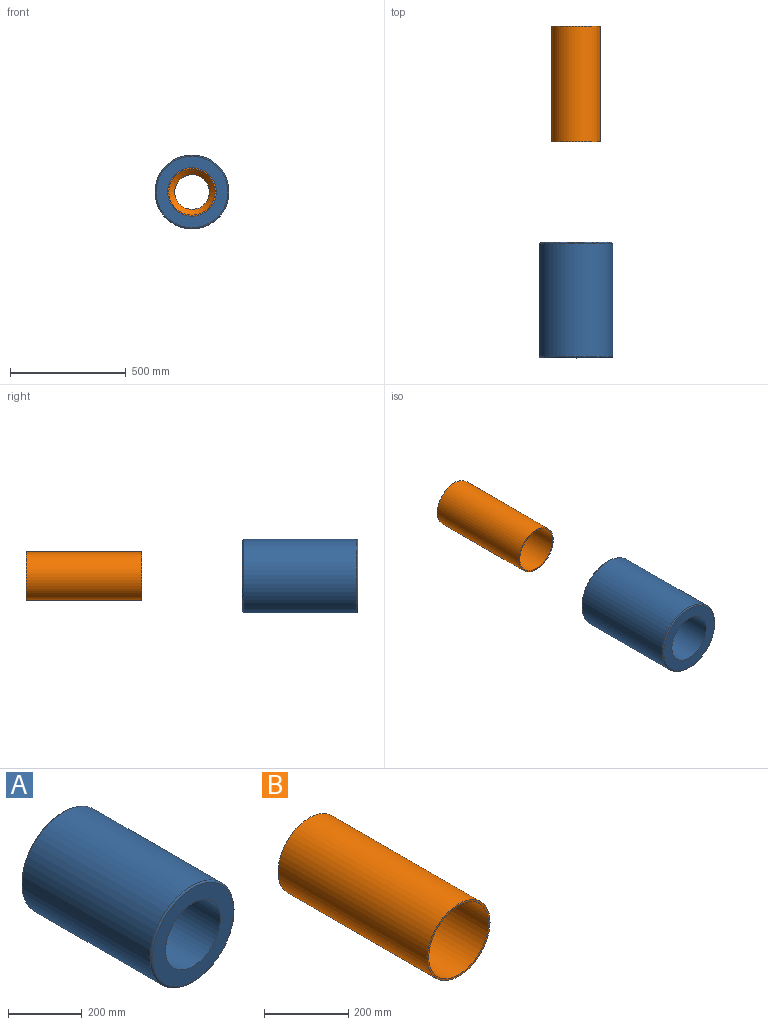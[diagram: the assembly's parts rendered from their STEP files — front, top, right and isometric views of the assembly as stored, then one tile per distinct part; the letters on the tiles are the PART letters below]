
ASSEMBLY  parts=2 mates=1
PART A: 6 faces, bbox 346.4x500x346.4 mm
  f0: cylinder r=160mm len=490mm, axis (0,1,0), area 492601.7mm2, adj f4,f5
  f1: plane 310x310mm, normal (0,-1,0), area 40840.7mm2, adj f3,f4
  f2: plane 310x310mm, normal (0,1,0), area 40840.7mm2, adj f3,f5
  f3: cylinder r=105mm len=500mm, axis (0,-1,0), area 329867.2mm2, adj f1,f2
  f4: torus R=155mm, axis (0,-1,0), area 7806mm2, adj f0,f1
  f5: cone r=160mm half-angle=45deg, axis (0,-1,0), area 6997.5mm2, adj f0,f2
PART B: 47 faces, bbox 210x500x210 mm
  f0: cylinder r=75mm len=315mm, axis (0,1,0), area 148440.3mm2, adj f45,f46
  f1: cylinder r=105mm len=500mm, axis (0,-1,0), area 329867.2mm2, adj f2,f3
  f2: plane 210x210mm, normal (0,-1,0), area 3220.1mm2, adj f1,f44
  f3: plane 210x210mm, normal (0,1,0), area 12075.5mm2, adj f1,f4,f6,f8,f10,f12,f14,f16
  f4: cylinder r=6.25mm len=300mm, axis (0,1,0), area 11781mm2, adj f3,f5
  f5: plane 12.5x12.5mm, normal (0,1,0), area 122.7mm2, adj f4
  f6: cylinder r=6.25mm len=300mm, axis (0,1,0), area 11781mm2, adj f3,f7
  f7: plane 12.5x12.5mm, normal (0,1,0), area 122.7mm2, adj f6
  f8: cylinder r=6.25mm len=300mm, axis (0,1,0), area 11781mm2, adj f3,f9
  f9: plane 12.5x12.5mm, normal (0,1,0), area 122.7mm2, adj f8
  f10: cylinder r=6.25mm len=300mm, axis (0,1,0), area 11781mm2, adj f3,f11
  f11: plane 12.5x12.5mm, normal (0,1,0), area 122.7mm2, adj f10
  f12: cylinder r=6.25mm len=300mm, axis (0,1,0), area 11781mm2, adj f3,f13
  f13: plane 12.5x12.5mm, normal (0,1,0), area 122.7mm2, adj f12
  f14: cylinder r=6.25mm len=300mm, axis (0,1,0), area 11781mm2, adj f3,f15
  f15: plane 12.5x12.5mm, normal (0,1,0), area 122.7mm2, adj f14
  f16: cylinder r=6.25mm len=300mm, axis (0,1,0), area 11781mm2, adj f3,f17
  f17: plane 12.5x12.5mm, normal (0,1,0), area 122.7mm2, adj f16
  f18: cylinder r=6.25mm len=300mm, axis (0,1,0), area 11781mm2, adj f3,f19
  f19: plane 12.5x12.5mm, normal (0,1,0), area 122.7mm2, adj f18
  f20: cylinder r=6.25mm len=300mm, axis (0,1,0), area 11781mm2, adj f3,f21
  f21: plane 12.5x12.5mm, normal (0,1,0), area 122.7mm2, adj f20
  f22: cylinder r=6.25mm len=300mm, axis (0,1,0), area 11781mm2, adj f3,f23
  f23: plane 12.5x12.5mm, normal (0,1,0), area 122.7mm2, adj f22
  f24: cylinder r=6.25mm len=300mm, axis (0,1,0), area 11781mm2, adj f3,f25
  f25: plane 12.5x12.5mm, normal (0,1,0), area 122.7mm2, adj f24
  f26: cylinder r=6.25mm len=300mm, axis (0,1,0), area 11781mm2, adj f3,f27
  f27: plane 12.5x12.5mm, normal (0,1,0), area 122.7mm2, adj f26
  f28: cylinder r=6.25mm len=300mm, axis (0,1,0), area 11781mm2, adj f3,f29
  f29: plane 12.5x12.5mm, normal (0,1,0), area 122.7mm2, adj f28
  f30: cylinder r=6.25mm len=300mm, axis (0,1,0), area 11781mm2, adj f3,f31
  f31: plane 12.5x12.5mm, normal (0,1,0), area 122.7mm2, adj f30
  f32: cylinder r=6.25mm len=300mm, axis (0,1,0), area 11781mm2, adj f3,f33
  f33: plane 12.5x12.5mm, normal (0,1,0), area 122.7mm2, adj f32
  f34: cylinder r=6.25mm len=300mm, axis (0,1,0), area 11781mm2, adj f3,f35
  f35: plane 12.5x12.5mm, normal (0,1,0), area 122.7mm2, adj f34
  f36: cylinder r=6.25mm len=300mm, axis (0,1,0), area 11781mm2, adj f3,f37
  f37: plane 12.5x12.5mm, normal (0,1,0), area 122.7mm2, adj f36
  f38: cylinder r=6.25mm len=300mm, axis (0,1,0), area 11781mm2, adj f3,f39
  f39: plane 12.5x12.5mm, normal (0,1,0), area 122.7mm2, adj f38
  f40: cylinder r=6.25mm len=300mm, axis (0,1,0), area 11781mm2, adj f3,f41
  f41: plane 12.5x12.5mm, normal (0,1,0), area 122.7mm2, adj f40
  f42: cylinder r=6.25mm len=300mm, axis (0,1,0), area 11781mm2, adj f3,f43
  f43: plane 12.5x12.5mm, normal (0,1,0), area 122.7mm2, adj f42
  f44: cylinder r=100mm len=200mm, axis (0,-1,0), area 97389.4mm2, adj f2,f45
  f45: cone r=75mm half-angle=45deg, axis (0,-1,0), area 19437.6mm2, adj f0,f44
  f46: cone r=75mm half-angle=45deg, axis (0,1,0), area 3443.2mm2, adj f0,f3
PLACE A t=(164.88,-257.49,197.86)mm
PLACE B t=(164.88,678.06,197.86)mm
MATE cylindrical A.f0 <-> B.f0  axis (0,-1,0) through (164.88,-507.49,197.86)mm
